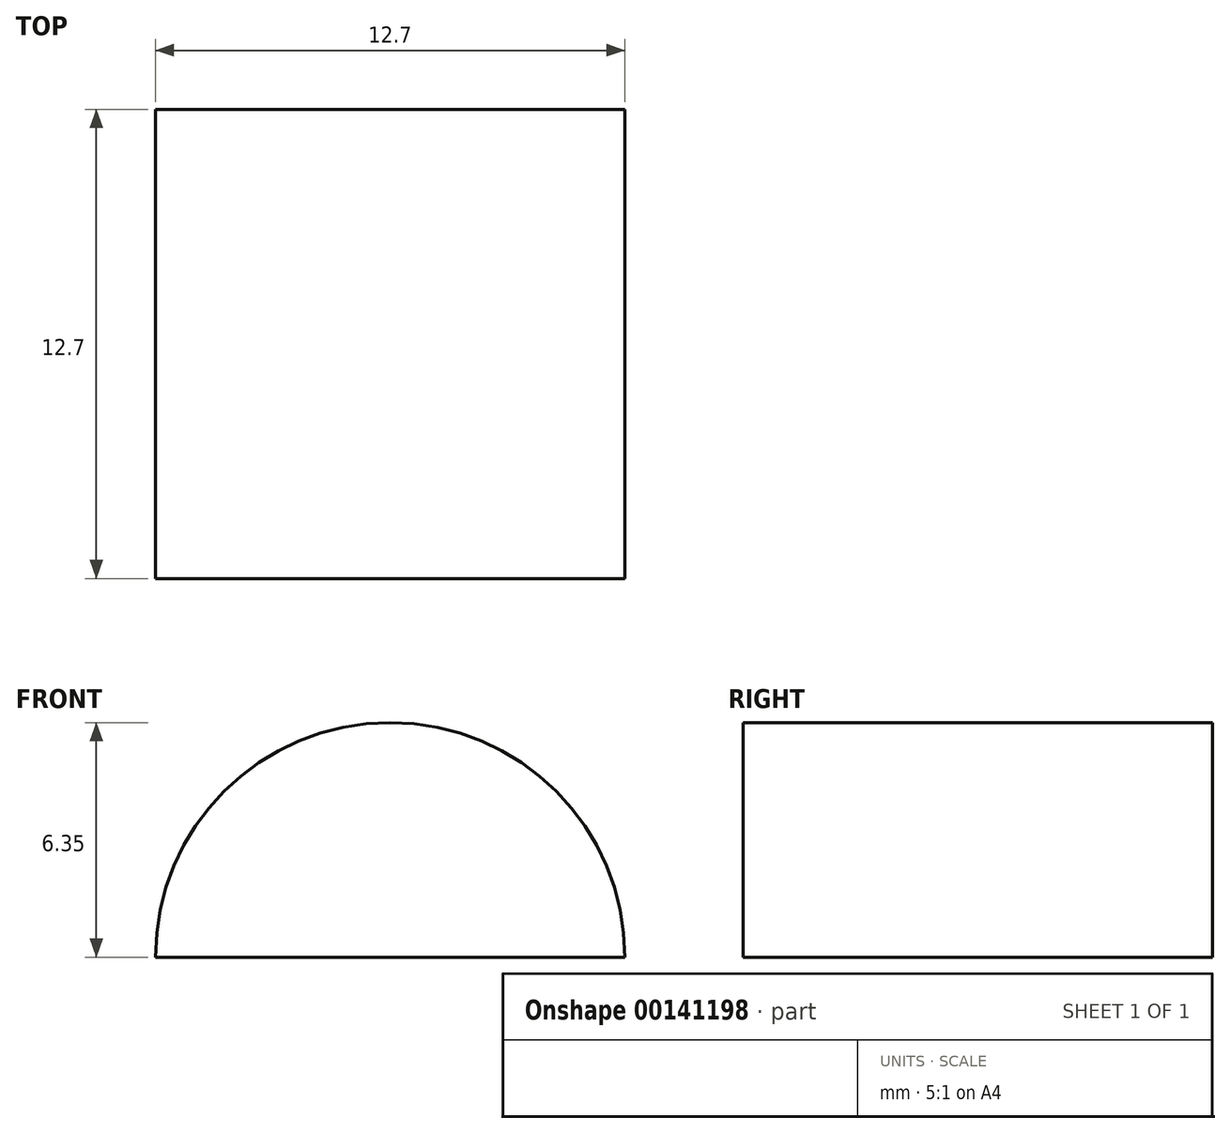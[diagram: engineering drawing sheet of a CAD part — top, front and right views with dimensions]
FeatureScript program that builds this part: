
annotation { "Feature Type Name" : "Feature", "Feature Type Description" : "" }
export const myFeature = defineFeature(function(context is Context, id is Id, definition is map)
    precondition{}
    {
        {
            var Q0;
            Q0=qCreatedBy(makeId("Front.planeOp"),FACE);
            var sketch = newSketch(context, id + "F0", { "sketchPlane" : qUnion([Q0])});
            skArc(sketch, "E0", {"start": v(6.35, 0) * mm, "mid": v(0, 6.35) * mm, "end": v(-6.35, 0) * mm});
            skLineSegment(sketch, "E1", {"start": v(-6.35, 0) * mm, "end": v(6.35, 0) * mm});
            skSolve(sketch);
        }
        {
            var Q0;
            Q0=makeQuery(id+"F0.imprint","IMPRINT",FACE,{"disambiguationData":[TD([[makeQuery(id+"F0.imprint","IMPRINT",EDGE,{"derivedFrom":sQuery(id+"F0.wireOp",EDGE,"E0")}),1.0]])]});
            extrude(context, id + "F1", {"entities" : qUnion([Q0]), "depth" : 12.7 * mm});
        }
    });
